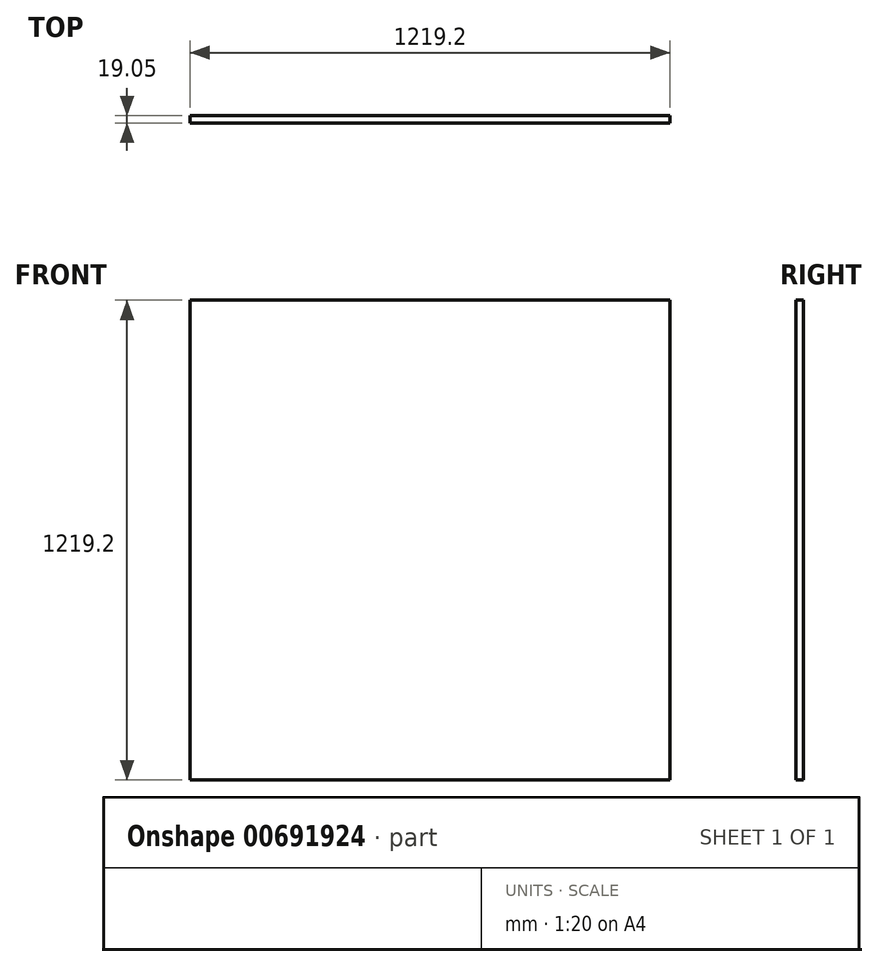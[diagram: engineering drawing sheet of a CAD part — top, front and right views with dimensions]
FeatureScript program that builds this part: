
annotation { "Feature Type Name" : "Feature", "Feature Type Description" : "" }
export const myFeature = defineFeature(function(context is Context, id is Id, definition is map)
    precondition{}
    {
        {
            var Q0;
            Q0=qCreatedBy(makeId("Front.planeOp"),FACE);
            var sketch = newSketch(context, id + "F0", { "sketchPlane" : qUnion([Q0])});
            skLineSegment(sketch, "E0.bottom", {"start": v(0, 0) * mm, "end": v(1219.2, 0) * mm});
            skLineSegment(sketch, "E0.top", {"start": v(0, 1219.2) * mm, "end": v(1219.2, 1219.2) * mm});
            skLineSegment(sketch, "E0.left", {"start": v(0, 0) * mm, "end": v(0, 1219.2) * mm});
            skLineSegment(sketch, "E0.right", {"start": v(1219.2, 0) * mm, "end": v(1219.2, 1219.2) * mm});
            skSolve(sketch);
        }
        {
            var Q0;
            Q0=makeQuery(id+"F0.imprint","IMPRINT",FACE,{"disambiguationData":[TD([[makeQuery(id+"F0.imprint","IMPRINT",EDGE,{"derivedFrom":sQuery(id+"F0.wireOp",EDGE,"E0.bottom")}),1.0]])]});
            extrude(context, id + "F1", {"entities" : qUnion([Q0]), "depth" : 19.05 * mm, "offsetDistance" : 25.4 * mm});
        }
    });
